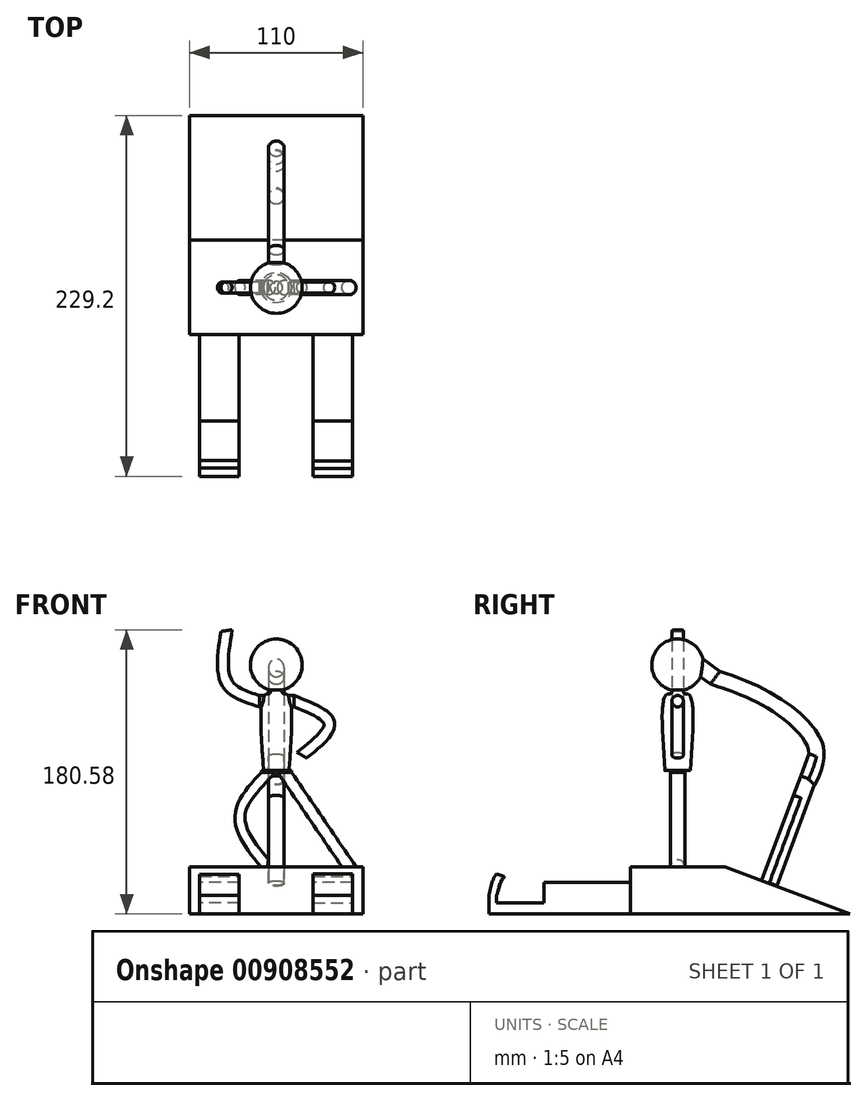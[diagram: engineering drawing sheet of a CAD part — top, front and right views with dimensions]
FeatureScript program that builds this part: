
annotation { "Feature Type Name" : "Feature", "Feature Type Description" : "" }
export const myFeature = defineFeature(function(context is Context, id is Id, definition is map)
    precondition{}
    {
        {
            var Q0;
            Q0=qCreatedBy(makeId("Front.planeOp"),FACE);
            var sketch = newSketch(context, id + "F0", { "sketchPlane" : qUnion([Q0])});
            skLineSegment(sketch, "E0", {"start": v(0, 69.26) * mm, "end": v(0, 36.4) * mm});
            skArc(sketch, "E1", {"start": v(0, 36.4) * mm, "mid": v(-16.43, 52.83) * mm, "end": v(0, 69.26) * mm});
            skSolve(sketch);
        }
        {
            var Q0;
            Q0=makeQuery(id+"F0.imprint","IMPRINT",FACE,{"disambiguationData":[TD([[makeQuery(id+"F0.imprint","IMPRINT",EDGE,{"derivedFrom":sQuery(id+"F0.wireOp",EDGE,"E0")}),-1.0]])]});
            var Q1;
            Q1=sQuery(id+"F0.wireOp",EDGE,"E0");
            revolve(context, id + "F1", {"surfaceOperationType" : NewSurfaceOperationType.NEW, "entities" : qUnion([Q0]), "axis" : qUnion([Q1]), "revolveType" : RevolveType.FULL});
        }
        {
            var Q0;
            Q0=qCreatedBy(makeId("Front.planeOp"),FACE);
            var sketch = newSketch(context, id + "F2", { "sketchPlane" : qUnion([Q0])});
            skLineSegment(sketch, "E2", {"start": v(0, 35.83) * mm, "end": v(0, -11.19) * mm});
            skLineSegment(sketch, "E3", {"start": v(0, -13.17) * mm, "end": v(0, -11.19) * mm});
            skLineSegment(sketch, "E4", {"start": v(0, 35.83) * mm, "end": v(0, 37.77) * mm});
            skLineSegment(sketch, "E5", {"start": v(0, 37.77) * mm, "end": v(-4.1, 38.1) * mm});
            skFitSpline(sketch, "E6", {"points": [v(-4.1, 38.1) * mm, v(-4.1, 34.7) * mm, v(-7.22, 33.85) * mm, v(-8.07, -14.3) * mm], "startDerivative": vector(5.22, -25.1) * mm, "endDerivative": vector(7.5, -102.76) * mm});
            skLineSegment(sketch, "E7", {"start": v(-8.07, -14.3) * mm, "end": v(0, -14.3) * mm});
            skLineSegment(sketch, "E8", {"start": v(0, -14.3) * mm, "end": v(0, -13.17) * mm});
            skSolve(sketch);
        }
        {
            var Q0;
            Q0=makeQuery(id+"F2.imprint","IMPRINT",FACE,{"disambiguationData":[TD([[makeQuery(id+"F2.imprint","IMPRINT",EDGE,{"derivedFrom":sQuery(id+"F2.wireOp",EDGE,"E2")}),-1.0]])]});
            var Q1;
            Q1=sQuery(id+"F2.wireOp",EDGE,"E2");
            revolve(context, id + "F3", {"operationType" : NewBodyOperationType.ADD, "surfaceOperationType" : NewSurfaceOperationType.NEW, "entities" : qUnion([Q0]), "axis" : qUnion([Q1]), "revolveType" : RevolveType.FULL});
        }
        {
            var Q0;
            Q0=qCreatedBy(makeId("Right.planeOp"),FACE);
            var sketch = newSketch(context, id + "F4", { "sketchPlane" : qUnion([Q0])});
            skCircle(sketch, "E9", {"center": v(0, 29.74) * mm, "radius": 3.62 * mm});
            skSolve(sketch);
        }
        {
            var Q0;
            Q0 = qSketchRegion(id + "F4", true);
            extrude(context, id + "F5", {"entities" : qUnion([Q0]), "operationType" : NewBodyOperationType.ADD, "oppositeDirection" : true, "depth" : 10.5 * mm, "offsetDistance" : 25 * mm});
        }
        {
            var Q0;
            Q0=qCreatedBy(makeId("Front.planeOp"),FACE);
            var sketch = newSketch(context, id + "F6", { "sketchPlane" : qUnion([Q0])});
            skLineSegment(sketch, "E10", {"start": v(0, 29.43) * mm, "end": v(-11.61, 29.43) * mm});
            skFitSpline(sketch, "E11", {"points": [v(-11.61, 29.43) * mm, v(-31.81, 40.98) * mm, v(-32.12, 75.66) * mm], "startDerivative": vector(-54.85, 17.22) * mm, "endDerivative": vector(11.63, 73.4) * mm});
            skSolve(sketch);
        }
        {
            var Q0;
            Q0=makeQuery(id+"F5.opExtrude","CAP_FACE",FACE,{"disambiguationData":[OSD([sQuery(id+"F4.wireOp",EDGE,"E9")])],"isStart":false});
            var Q1;
            Q1=sQuery(id+"F6.wireOp",EDGE,"E11");
            sweep(context, id + "F7", {"operationType" : NewBodyOperationType.ADD, "profiles" : qUnion([Q0]), "path" : qUnion([Q1])});
        }
        {
            var Q0;
            Q0 = qSketchRegion(id + "F4", true);
            extrude(context, id + "F8", {"entities" : qUnion([Q0]), "operationType" : NewBodyOperationType.ADD, "depth" : 11.2 * mm, "offsetDistance" : 25 * mm});
        }
        {
            var Q0;
            Q0=qCreatedBy(makeId("Front.planeOp"),FACE);
            var sketch = newSketch(context, id + "F9", { "sketchPlane" : qUnion([Q0])});
            skLineSegment(sketch, "E12", {"start": v(0, 29.43) * mm, "end": v(11.87, 29.43) * mm});
            skFitSpline(sketch, "E13", {"points": [v(11.87, 29.43) * mm, v(33.45, 15.62) * mm, v(15.55, -4.95) * mm], "startDerivative": vector(63.3, -24.98) * mm, "endDerivative": vector(-55.33, -43.68) * mm});
            skSolve(sketch);
        }
        {
            var Q0;
            Q0=makeQuery(id+"F8.opExtrude","CAP_FACE",FACE,{"disambiguationData":[OSD([sQuery(id+"F4.wireOp",EDGE,"E9")])],"isStart":false});
            var Q1;
            Q1=sQuery(id+"F9.wireOp",EDGE,"E13");
            sweep(context, id + "F10", {"operationType" : NewBodyOperationType.ADD, "profiles" : qUnion([Q0]), "path" : qUnion([Q1])});
        }
        {
            var Q0;
            Q0=makeQuery(id+"F3.opRevolve","SWEPT_FACE",FACE,{"disambiguationData":[OSD([sQuery(id+"F2.wireOp",EDGE,"E7")])]});
            var sketch = newSketch(context, id + "F11", { "sketchPlane" : qUnion([Q0])});
            skCircle(sketch, "E14", {"center": v(-4.96, 0) * mm, "radius": 4.5 * mm});
            skCircle(sketch, "E15", {"center": v(5.17, 0) * mm, "radius": 4.5 * mm});
            skSolve(sketch);
        }
        {
            var Q0;
            Q0 = qSketchRegion(id + "F11", true);
            extrude(context, id + "F12", {"entities" : qUnion([Q0]), "operationType" : NewBodyOperationType.ADD, "depth" : 1 * mm, "offsetDistance" : 25 * mm});
        }
        {
            var Q0;
            Q0=qCreatedBy(makeId("Front.planeOp"),FACE);
            var sketch = newSketch(context, id + "F13", { "sketchPlane" : qUnion([Q0])});
            skLineSegment(sketch, "E16", {"start": v(-5.28, -12.64) * mm, "end": v(5.22, -12.64) * mm});
            skLineSegment(sketch, "E17", {"start": v(5.22, -12.64) * mm, "end": v(5.22, -15.64) * mm});
            skLineSegment(sketch, "E18", {"start": v(-5.28, -12.64) * mm, "end": v(-5.28, -15.64) * mm});
            skFitSpline(sketch, "E19", {"points": [v(-5.28, -15.64) * mm, v(-22.9, -43.91) * mm, v(-5.28, -75.78) * mm], "startDerivative": vector(-53.28, -56.73) * mm, "endDerivative": vector(52.5, -63.5) * mm});
            skFitSpline(sketch, "E20", {"points": [v(5.22, -15.64) * mm, v(46.24, -75.78) * mm], "startDerivative": vector(41.02, -60.14) * mm, "endDerivative": vector(41.02, -60.14) * mm});
            skSolve(sketch);
        }
        {
            var Q0;
            Q0=makeQuery(id+"F12.opExtrude","CAP_FACE",FACE,{"disambiguationData":[OSD([sQuery(id+"F11.wireOp",EDGE,"E14")])],"isStart":false});
            var Q1;
            Q1=sQuery(id+"F13.wireOp",EDGE,"E19");
            sweep(context, id + "F14", {"operationType" : NewBodyOperationType.ADD, "profiles" : qUnion([Q0]), "path" : qUnion([Q1])});
        }
        {
            var Q0;
            Q0=makeQuery(id+"F12.opExtrude","CAP_FACE",FACE,{"disambiguationData":[OSD([sQuery(id+"F11.wireOp",EDGE,"E15")])],"isStart":false});
            var Q1;
            Q1=sQuery(id+"F13.wireOp",EDGE,"E20");
            sweep(context, id + "F15", {"operationType" : NewBodyOperationType.ADD, "profiles" : qUnion([Q0]), "path" : qUnion([Q1])});
        }
        {
            var Q0;
            Q0=makeQuery(id+"F15.opSweep","CAP_FACE",FACE,{"disambiguationData":[OSD([sQuery(id+"F11.wireOp",EDGE,"E15"),sQuery(id+"F13.wireOp",VERTEX,"E20.end")])],"isStart":false});
            var sketch = newSketch(context, id + "F16", { "sketchPlane" : qUnion([Q0])});
            skLineSegment(sketch, "E21.bottom", {"start": v(55, 30) * mm, "end": v(-55, 30) * mm});
            skLineSegment(sketch, "E21.top", {"start": v(55, -30) * mm, "end": v(-55, -30) * mm});
            skLineSegment(sketch, "E21.left", {"start": v(55, 30) * mm, "end": v(55, -30) * mm});
            skLineSegment(sketch, "E21.right", {"start": v(-55, 30) * mm, "end": v(-55, -30) * mm});
            skPoint(sketch, "E21.middle", {"position": v(0, 0) * mm});
            skSolve(sketch);
        }
        {
            var Q0;
            Q0=makeQuery(id+"F16.imprint","IMPRINT",FACE,{"disambiguationData":[TD([[makeQuery(id+"F16.imprint","IMPRINT",EDGE,{"derivedFrom":sQuery(id+"F16.wireOp",EDGE,"E21.bottom")}),1.0]])]});
            var Q1;
            Q1=makeQuery(id+"F16.imprint","IMPRINT",FACE,{"disambiguationData":[TD([[makeQuery(id+"F16.imprint","IMPRINT",EDGE,{"derivedFrom":makeQuery(id+"F15.opSweep","CAP_EDGE",EDGE,{"disambiguationData":[OSD([sQuery(id+"F11.wireOp",EDGE,"E15"),sQuery(id+"F13.wireOp",VERTEX,"E20.end")])],"isStart":false})}),1.0]])]});
            extrude(context, id + "F17", {"entities" : qUnion([Q0, Q1]), "operationType" : NewBodyOperationType.ADD, "depth" : 30 * mm, "offsetDistance" : 25 * mm});
        }
        {
            var Q0;
            Q0=makeQuery(id+"F17.opExtrude","SWEPT_FACE",FACE,{"disambiguationData":[OSD([sQuery(id+"F16.wireOp",EDGE,"E21.right")])]});
            var sketch = newSketch(context, id + "F18", { "sketchPlane" : qUnion([Q0])});
            skLineSegment(sketch, "E22", {"start": v(0, -105.44) * mm, "end": v(-109.3, -105.44) * mm});
            skLineSegment(sketch, "E23", {"start": v(-109.3, -105.44) * mm, "end": v(-30, -75.44) * mm});
            skSolve(sketch);
        }
        {
            var Q0;
            {var subQ2=sQuery(id+"F18.wireOp",EDGE,"E23");Q0=makeQuery(id+"F18.imprint","IMPRINT",FACE,{"disambiguationData":[TD([[makeQuery(id+"F18.imprint","IMPRINT",EDGE,{"derivedFrom":subQ2}),-1.0]])]});}
            extrude(context, id + "F19", {"entities" : qUnion([Q0]), "operationType" : NewBodyOperationType.ADD, "oppositeDirection" : true, "depth" : 110 * mm, "offsetDistance" : 25 * mm});
        }
        {
            var Q0;
            Q0=makeQuery(id+"F19.opExtrude","SWEPT_FACE",FACE,{"disambiguationData":[OSD([sQuery(id+"F18.wireOp",EDGE,"E23")])]});
            var sketch = newSketch(context, id + "F20", { "sketchPlane" : qUnion([Q0])});
            skCircle(sketch, "E24", {"center": v(0, 84.51) * mm, "radius": 5 * mm});
            skSolve(sketch);
        }
        {
            var Q0;
            Q0 = qSketchRegion(id + "F20", true);
            extrude(context, id + "F21", {"entities" : qUnion([Q0]), "operationType" : NewBodyOperationType.ADD, "depth" : 58 * mm, "offsetDistance" : 25 * mm});
        }
        {
            var Q0;
            Q0=qCreatedBy(makeId("Right.planeOp"),FACE);
            var sketch = newSketch(context, id + "F22", { "sketchPlane" : qUnion([Q0])});
            skLineSegment(sketch, "E25", {"start": v(58.16, -85.61) * mm, "end": v(82.6, -19.3) * mm});
            skFitSpline(sketch, "E26", {"points": [v(82.6, -19.3) * mm, v(86.48, 0) * mm, v(64.87, 24.54) * mm, v(38.22, 38.33) * mm, v(23.04, 43.6) * mm], "startDerivative": vector(37.04, 83.9) * mm, "endDerivative": vector(-69.8, 22.53) * mm});
            skSolve(sketch);
        }
        {
            var Q0;
            Q0=makeQuery(id+"F21.opExtrude","CAP_FACE",FACE,{"disambiguationData":[OSD([sQuery(id+"F20.wireOp",EDGE,"E24")])],"isStart":false});
            var Q1;
            Q1=sQuery(id+"F22.wireOp",EDGE,"E25");
            var Q2;
            Q2=sQuery(id+"F22.wireOp",EDGE,"64380822-9af3-4c74-a5a6-4e8d5d2d115b");
            sweep(context, id + "F23", {"operationType" : NewBodyOperationType.ADD, "profiles" : qUnion([Q0]), "path" : qUnion([Q1, Q2])});
        }
        {
            var Q0;
            Q0=makeQuery(id+"F23.opSweep","CAP_FACE",FACE,{"disambiguationData":[OSD([sQuery(id+"F20.wireOp",EDGE,"E24"),sQuery(id+"F22.wireOp",VERTEX,"64380822-9af3-4c74-a5a6-4e8d5d2d115b.end")])],"isStart":false});
            extrude(context, id + "F24", {"entities" : qUnion([Q0]), "operationType" : NewBodyOperationType.ADD, "depth" : 15 * mm, "offsetDistance" : 25 * mm});
        }
        {
            var Q0;
            Q0=makeQuery(id+"F17.opExtrude","SWEPT_FACE",FACE,{"disambiguationData":[OSD([sQuery(id+"F16.wireOp",EDGE,"E21.bottom")])]});
            var sketch = newSketch(context, id + "F25", { "sketchPlane" : qUnion([Q0])});
            skLineSegment(sketch, "E27.bottom", {"start": v(-23.6, -105.44) * mm, "end": v(-48.6, -105.44) * mm});
            skLineSegment(sketch, "E27.top", {"start": v(-23.6, -85.44) * mm, "end": v(-48.6, -85.44) * mm});
            skLineSegment(sketch, "E27.left", {"start": v(-23.6, -105.44) * mm, "end": v(-23.6, -85.44) * mm});
            skLineSegment(sketch, "E27.right", {"start": v(-48.6, -105.44) * mm, "end": v(-48.6, -85.44) * mm});
            skPoint(sketch, "E27.middle", {"position": v(-36.1, -95.44) * mm});
            skLineSegment(sketch, "E28.bottom", {"start": v(48.4, -85.44) * mm, "end": v(23.4, -85.44) * mm});
            skLineSegment(sketch, "E28.top", {"start": v(48.4, -105.44) * mm, "end": v(23.4, -105.44) * mm});
            skLineSegment(sketch, "E28.left", {"start": v(48.4, -85.44) * mm, "end": v(48.4, -105.44) * mm});
            skLineSegment(sketch, "E28.right", {"start": v(23.4, -85.44) * mm, "end": v(23.4, -105.44) * mm});
            skPoint(sketch, "E28.middle", {"position": v(35.9, -95.44) * mm});
            skSolve(sketch);
        }
        {
            var Q0;
            Q0=makeQuery(id+"F25.imprint","IMPRINT",FACE,{"disambiguationData":[TD([[makeQuery(id+"F25.imprint","IMPRINT",EDGE,{"derivedFrom":sQuery(id+"F25.wireOp",EDGE,"E28.bottom")}),1.0]])]});
            var Q1;
            Q1=makeQuery(id+"F25.imprint","IMPRINT",FACE,{"disambiguationData":[TD([[makeQuery(id+"F25.imprint","IMPRINT",EDGE,{"derivedFrom":sQuery(id+"F25.wireOp",EDGE,"E27.bottom")}),-1.0]])]});
            extrude(context, id + "F26", {"entities" : qUnion([Q0, Q1]), "operationType" : NewBodyOperationType.ADD, "depth" : 54.9 * mm, "offsetDistance" : 25 * mm});
        }
        {
            var Q0;
            Q0=makeQuery(id+"F26.opExtrude","CAP_FACE",FACE,{"disambiguationData":[OSD([sQuery(id+"F25.wireOp",EDGE,"E27.bottom"),sQuery(id+"F25.wireOp",EDGE,"E27.top"),sQuery(id+"F25.wireOp",EDGE,"E27.left"),sQuery(id+"F25.wireOp",EDGE,"E27.right")])],"isStart":false});
            var sketch = newSketch(context, id + "F27", { "sketchPlane" : qUnion([Q0])});
            skLineSegment(sketch, "E29", {"start": v(-48.6, -98.44) * mm, "end": v(-48.6, -105.44) * mm});
            skLineSegment(sketch, "E30", {"start": v(-48.6, -105.44) * mm, "end": v(-23.6, -105.44) * mm});
            skLineSegment(sketch, "E31", {"start": v(-23.6, -105.44) * mm, "end": v(-23.6, -98.44) * mm});
            skLineSegment(sketch, "E32", {"start": v(-23.6, -98.44) * mm, "end": v(-48.6, -98.44) * mm});
            skSolve(sketch);
        }
        {
            var Q0;
            Q0=makeQuery(id+"F27.imprint","IMPRINT",FACE,{"disambiguationData":[TD([[makeQuery(id+"F27.imprint","IMPRINT",EDGE,{"derivedFrom":sQuery(id+"F27.wireOp",EDGE,"E29")}),-1.0]])]});
            extrude(context, id + "F28", {"entities" : qUnion([Q0]), "operationType" : NewBodyOperationType.ADD, "depth" : 35 * mm, "offsetDistance" : 25 * mm});
        }
        {
            var Q0;
            Q0=makeQuery(id+"F26.opExtrude","CAP_FACE",FACE,{"disambiguationData":[OSD([sQuery(id+"F25.wireOp",EDGE,"E28.bottom"),sQuery(id+"F25.wireOp",EDGE,"E28.top"),sQuery(id+"F25.wireOp",EDGE,"E28.left"),sQuery(id+"F25.wireOp",EDGE,"E28.right")])],"isStart":false});
            var sketch = newSketch(context, id + "F29", { "sketchPlane" : qUnion([Q0])});
            skLineSegment(sketch, "E33", {"start": v(23.4, -105.44) * mm, "end": v(23.4, -98.44) * mm});
            skLineSegment(sketch, "E34", {"start": v(23.4, -98.44) * mm, "end": v(48.4, -98.44) * mm});
            skLineSegment(sketch, "E35", {"start": v(48.4, -98.44) * mm, "end": v(48.4, -105.44) * mm});
            skLineSegment(sketch, "E36", {"start": v(48.4, -105.44) * mm, "end": v(23.4, -105.44) * mm});
            skSolve(sketch);
        }
        {
            var Q0;
            Q0=makeQuery(id+"F29.imprint","IMPRINT",FACE,{"disambiguationData":[TD([[makeQuery(id+"F29.imprint","IMPRINT",EDGE,{"derivedFrom":sQuery(id+"F29.wireOp",EDGE,"E33")}),1.0]])]});
            extrude(context, id + "F30", {"entities" : qUnion([Q0]), "operationType" : NewBodyOperationType.ADD, "depth" : 35 * mm, "offsetDistance" : 25 * mm});
        }
        {
            var Q0;
            Q0=makeQuery(id+"F30.opExtrude","SWEPT_FACE",FACE,{"disambiguationData":[OSD([sQuery(id+"F29.wireOp",EDGE,"E34")])]});
            var sketch = newSketch(context, id + "F31", { "sketchPlane" : qUnion([Q0])});
            skLineSegment(sketch, "E37", {"start": v(23.4, -119.9) * mm, "end": v(23.4, -114.9) * mm});
            skLineSegment(sketch, "E38", {"start": v(23.4, -114.9) * mm, "end": v(48.4, -114.9) * mm});
            skLineSegment(sketch, "E39", {"start": v(48.4, -114.9) * mm, "end": v(48.4, -119.9) * mm});
            skSolve(sketch);
        }
        {
            var Q0;
            Q0=makeQuery(id+"F31.imprint","IMPRINT",FACE,{"disambiguationData":[TD([[makeQuery(id+"F31.imprint","IMPRINT",EDGE,{"derivedFrom":sQuery(id+"F31.wireOp",EDGE,"E37")}),-1.0]])]});
            extrude(context, id + "F32", {"entities" : qUnion([Q0]), "operationType" : NewBodyOperationType.ADD, "depth" : 5 * mm, "offsetDistance" : 25 * mm});
        }
        {
            var Q0;
            Q0=makeQuery(id+"F28.opExtrude","SWEPT_FACE",FACE,{"disambiguationData":[OSD([sQuery(id+"F27.wireOp",EDGE,"E32")])]});
            var sketch = newSketch(context, id + "F33", { "sketchPlane" : qUnion([Q0])});
            skLineSegment(sketch, "E40", {"start": v(-48.6, -119.9) * mm, "end": v(-48.6, -114.9) * mm});
            skLineSegment(sketch, "E41", {"start": v(-48.6, -114.9) * mm, "end": v(-23.6, -114.9) * mm});
            skLineSegment(sketch, "E42", {"start": v(-23.6, -114.9) * mm, "end": v(-23.6, -119.9) * mm});
            skSolve(sketch);
        }
        {
            var Q0;
            Q0=makeQuery(id+"F33.imprint","IMPRINT",FACE,{"disambiguationData":[TD([[makeQuery(id+"F33.imprint","IMPRINT",EDGE,{"derivedFrom":sQuery(id+"F33.wireOp",EDGE,"E40")}),-1.0]])]});
            extrude(context, id + "F34", {"entities" : qUnion([Q0]), "operationType" : NewBodyOperationType.ADD, "depth" : 5 * mm, "offsetDistance" : 25 * mm});
        }
        {
            var Q0;
            Q0=makeQuery(id+"F34.boolean.opBoolean","MERGE",FACE,{"derivedFrom":[makeQuery(id+"F28.boolean.opBoolean","MERGE",FACE,{"derivedFrom":[makeQuery(id+"F26.opExtrude","SWEPT_FACE",FACE,{"disambiguationData":[OSD([sQuery(id+"F25.wireOp",EDGE,"E27.right")])]}),makeQuery(id+"F28.opExtrude","SWEPT_FACE",FACE,{"disambiguationData":[OSD([sQuery(id+"F27.wireOp",EDGE,"E29")])]})]}),makeQuery(id+"F34.opExtrude","SWEPT_FACE",FACE,{"disambiguationData":[OSD([sQuery(id+"F33.wireOp",EDGE,"E40")])]})]});
            var sketch = newSketch(context, id + "F35", { "sketchPlane" : qUnion([Q0])});
            skLineSegment(sketch, "E43", {"start": v(117.4, -100.55) * mm, "end": v(117.4, -90.54) * mm});
            skFitSpline(sketch, "E44", {"points": [v(117.4, -90.54) * mm, v(114.68, -83.2) * mm, v(111.53, -78.14) * mm], "startDerivative": vector(-4.62, 14.54) * mm, "endDerivative": vector(-7.16, 10.18) * mm});
            skSolve(sketch);
        }
        {
            var Q0;
            Q0=makeQuery(id+"F34.opExtrude","CAP_FACE",FACE,{"disambiguationData":[OSD([sQuery(id+"F27.wireOp",EDGE,"E32"),sQuery(id+"F33.wireOp",EDGE,"E40"),sQuery(id+"F33.wireOp",EDGE,"E41"),sQuery(id+"F33.wireOp",EDGE,"E42")])],"isStart":false});
            var Q1;
            Q1=sQuery(id+"F35.wireOp",EDGE,"E44");
            sweep(context, id + "F36", {"operationType" : NewBodyOperationType.ADD, "profiles" : qUnion([Q0]), "path" : qUnion([Q1])});
        }
        {
            var Q0;
            Q0=makeQuery(id+"F32.boolean.opBoolean","MERGE",FACE,{"derivedFrom":[makeQuery(id+"F30.boolean.opBoolean","MERGE",FACE,{"derivedFrom":[makeQuery(id+"F26.opExtrude","SWEPT_FACE",FACE,{"disambiguationData":[OSD([sQuery(id+"F25.wireOp",EDGE,"E28.left")])]}),makeQuery(id+"F30.opExtrude","SWEPT_FACE",FACE,{"disambiguationData":[OSD([sQuery(id+"F29.wireOp",EDGE,"E35")])]})]}),makeQuery(id+"F32.opExtrude","SWEPT_FACE",FACE,{"disambiguationData":[OSD([sQuery(id+"F31.wireOp",EDGE,"E39")])]})]});
            var sketch = newSketch(context, id + "F37", { "sketchPlane" : qUnion([Q0])});
            skLineSegment(sketch, "E45", {"start": v(-117.3, -100.2) * mm, "end": v(-117.3, -90.52) * mm});
            skFitSpline(sketch, "E46", {"points": [v(-117.3, -90.52) * mm, v(-114.87, -83.2) * mm, v(-111.57, -77.97) * mm], "startDerivative": vector(4, 14.6) * mm, "endDerivative": vector(7.54, 10.42) * mm});
            skSolve(sketch);
        }
        {
            var Q0;
            Q0=makeQuery(id+"F32.opExtrude","CAP_FACE",FACE,{"disambiguationData":[OSD([sQuery(id+"F29.wireOp",EDGE,"E34"),sQuery(id+"F31.wireOp",EDGE,"E37"),sQuery(id+"F31.wireOp",EDGE,"E38"),sQuery(id+"F31.wireOp",EDGE,"E39")])],"isStart":false});
            var Q1;
            Q1=sQuery(id+"F37.wireOp",EDGE,"E46");
            sweep(context, id + "F38", {"operationType" : NewBodyOperationType.ADD, "profiles" : qUnion([Q0]), "path" : qUnion([Q1])});
        }
        {
            var Q0;
            Q0=makeQuery(id+"F24.opExtrude","CAP_FACE",FACE,{"disambiguationData":[OSD([sQuery(id+"F20.wireOp",EDGE,"E24"),sQuery(id+"F22.wireOp",VERTEX,"E25.end")])],"isStart":false});
            var Q1;
            Q1=sQuery(id+"F22.wireOp",EDGE,"E26");
            sweep(context, id + "F39", {"operationType" : NewBodyOperationType.ADD, "profiles" : qUnion([Q0]), "path" : qUnion([Q1])});
        }
        {
            var Q0;
            Q0=makeQuery(id+"F39.opSweep","CAP_FACE",FACE,{"disambiguationData":[OSD([sQuery(id+"F20.wireOp",EDGE,"E24"),sQuery(id+"F22.wireOp",VERTEX,"E25.end"),sQuery(id+"F22.wireOp",VERTEX,"E26.end")])],"isStart":false});
            extrude(context, id + "F40", {"entities" : qUnion([Q0]), "operationType" : NewBodyOperationType.ADD, "depth" : 20 * mm, "offsetDistance" : 25 * mm});
        }
    });
